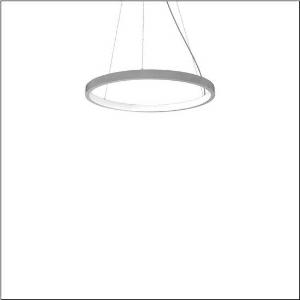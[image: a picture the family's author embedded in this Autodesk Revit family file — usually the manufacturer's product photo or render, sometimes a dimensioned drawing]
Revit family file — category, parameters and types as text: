
# Revit family: silica_r__21_ring-i_5pjbi2d1204a_a024
name_source: partatom
category: Lighting Fixtures
units: mm (PartAtom-declared; Revit-internal decimal feet)

## family parameters
Cut with Voids When Loaded = No
Host = Face
Light Source = No
Part Type = Normal
Room Calculation Point = No
Round Connector Dimension = Use Diameter
Shared = No

## types (1)
- Silica® 21 Ring-I (1 x LED, 4800 lm, 80 W, 3000K)
    Apparent Load = 80 VA
    CIE Flux Codes = 22 48 76 50 101
    Color Rendering = 80
    Color Temperature = 3000K
    Default Elevation = 1800 mm
    Description = Silica® 21 Ring-I, suspended luminaire, of PMMA, frosted, light emission: inner ring side luminous distribution, primary light characteristic: symmetric, installation type: suspended mounting, LED, rated luminous flux: 4.800lm, luminous efficacy: 60lm/W, light colour: 830, colour temperature: 3000K, control gear: DALI 2, with terminal, 5-pole, mains connection: 230V, AC/DC, 0/50..60Hz, rated input power: 80W, housing, of extruded aluminium section, metallic grey (RAL 9006), diameter: 805mm, ceiling canopy, metallic grey (RAL 9006), protection rating (lamp compartment): IP40, insulation class (complete): insulation class I (protective earthing), certification: CE, impact resistance: IK02, permissible operating ambient temperature: 0..+35°C, packaging unit: 1 piece
    Height = 48 mm  [stored 0.15748 ft]
    Lamp = 1 x LED
    Lamp Light Flux = 4800 lm
    Lamp Power = 80 W
    Lamp count = 1
    Length = 805 mm
    Luminous efficacy = 60 lm/W
    Manufacturer = Siteco
    ModVariant = No
    Model = 5PJBI2D1204A
    Mounting Place = Ceiling
    Mounting Type = Pendant
    Number of Poles = 1
    OnlyDefault = Yes
    Power Factor = 1
    Product Name = Silica® 21 Ring-I
    Product group = suspended luminaire
    ProductGroupID = 904
    Protection Class = Protection class I
    Protection Degree = IP 40
    RLX_Detail_Level = 1
    RLX_Emergency_Light_Flux = 0 lm
    RLX_Emergency_Type = 0
    RLX_Emergency_Type_DB = No
    RlxData = <blob elided: 13121 chars, md5=3bb4b488>
    Socket = socket
    Standby Power = 0 W
    System Light Flux = 4800 lm
    System Power = 80 W
    Type Comments = Product without accessories
    Type Image = l_1251752.jpg
    URL = http://relux.com
    VarID = ---
    Voltage = 0 V
    Weight = 0.00 kg
    Width = 0 mm  [stored 0 ft]

note: [stored X ft] marks values corroborated as IEEE doubles in the binary element streams (Revit-internal decimal feet)

## geometry (parser evidence)
native form markers: Sweep x13
no freeform markers — native parametric forms only
